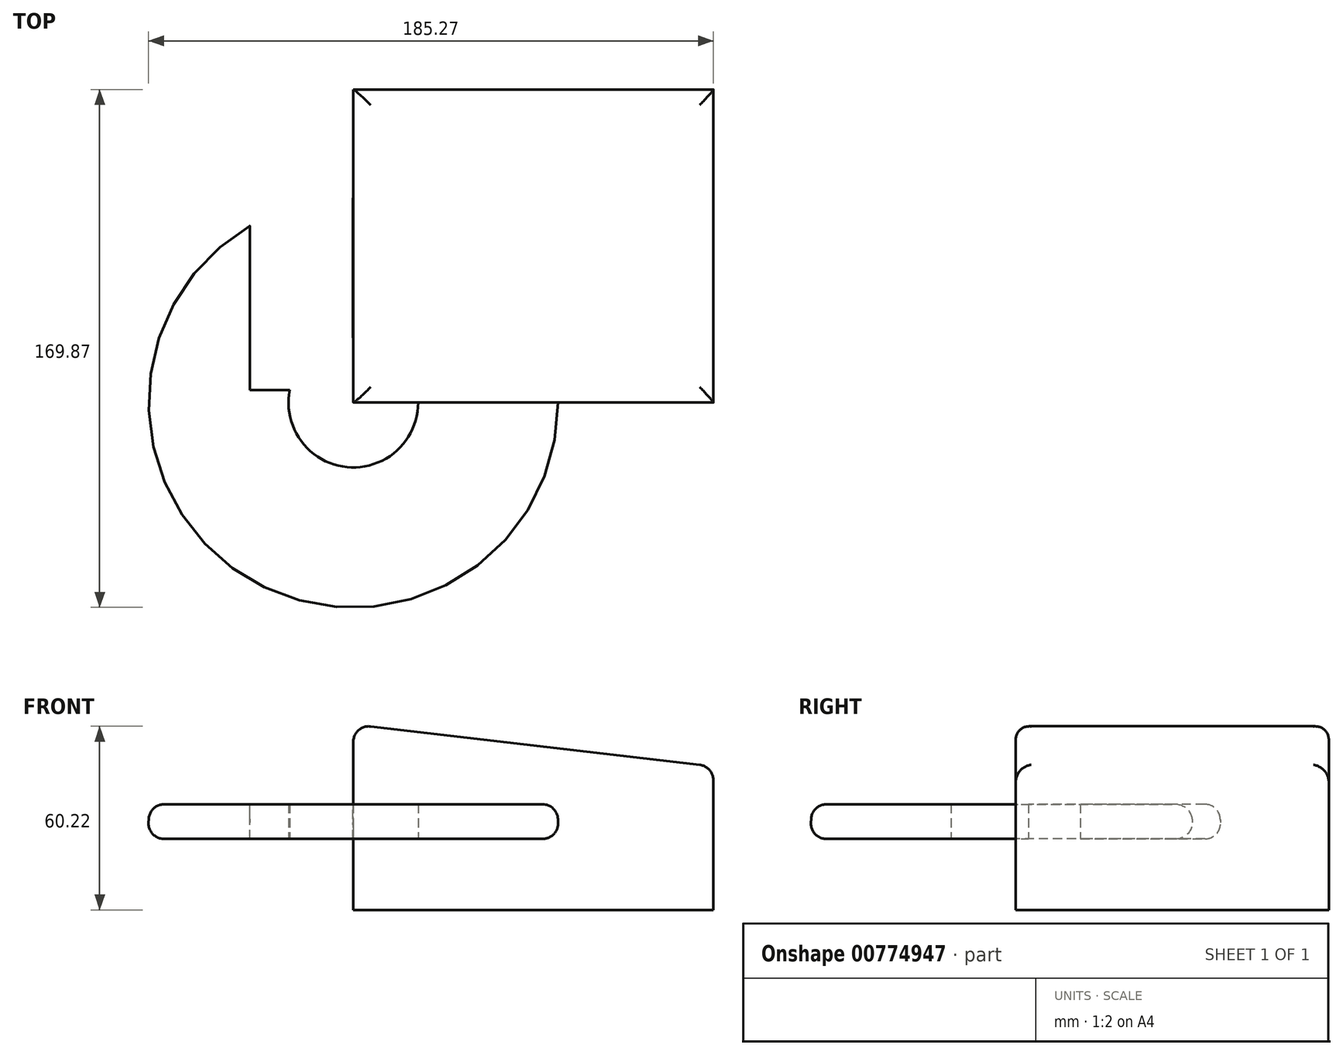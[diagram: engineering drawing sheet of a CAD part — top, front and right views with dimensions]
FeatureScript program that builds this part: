
annotation { "Feature Type Name" : "Feature", "Feature Type Description" : "" }
export const myFeature = defineFeature(function(context is Context, id is Id, definition is map)
    precondition{}
    {
        {
            var Q0;
            Q0=qCreatedBy(makeId("Front.planeOp"),FACE);
            var sketch = newSketch(context, id + "F0", { "sketchPlane" : qUnion([Q0])});
            skLineSegment(sketch, "E0", {"start": v(62.23, 12.4) * mm, "end": v(62.23, -34.65) * mm});
            skLineSegment(sketch, "E1", {"start": v(62.23, -34.65) * mm, "end": v(-55.87, -34.65) * mm});
            skLineSegment(sketch, "E2", {"start": v(-55.87, -34.65) * mm, "end": v(-55.87, 26.2) * mm});
            skLineSegment(sketch, "E3", {"start": v(-55.87, 26.2) * mm, "end": v(62.23, 12.4) * mm});
            skSolve(sketch);
        }
        {
            var Q0;
            Q0=makeQuery(id+"F0.imprint","IMPRINT",FACE,{"disambiguationData":[TD([[makeQuery(id+"F0.imprint","IMPRINT",EDGE,{"derivedFrom":sQuery(id+"F0.wireOp",EDGE,"E0")}),-1.0]])]});
            var Q1;
            Q1 = qSketchRegion(id + "F0", true);
            extrude(context, id + "F1", {"entities" : qUnion([Q0, Q1]), "depth" : 102.7 * mm, "offsetDistance" : 25.4 * mm});
        }
        {
            var Q0;
            Q0=makeQuery(id+"F1.opExtrude","CAP_FACE",FACE,{"disambiguationData":[OSD([sQuery(id+"F0.wireOp",EDGE,"E0"),sQuery(id+"F0.wireOp",EDGE,"E1"),sQuery(id+"F0.wireOp",EDGE,"E2"),sQuery(id+"F0.wireOp",EDGE,"E3")])],"isStart":false});
            var sketch = newSketch(context, id + "F2", { "sketchPlane" : qUnion([Q0])});
            skLineSegment(sketch, "E4", {"start": v(11.54, -11.35) * mm, "end": v(-34.62, -11.35) * mm});
            skLineSegment(sketch, "E5", {"start": v(-34.62, -11.35) * mm, "end": v(-34.62, 0) * mm});
            skLineSegment(sketch, "E6", {"start": v(-34.62, 0) * mm, "end": v(11.03, 0) * mm});
            skLineSegment(sketch, "E7", {"start": v(11.03, 0) * mm, "end": v(11.54, -11.35) * mm});
            skSolve(sketch);
        }
        {
            var Q0;
            Q0 = qSketchRegion(id + "F2", true);
            var Q1;
            Q1=makeQuery(id+"F1.opExtrude","CAP_EDGE",EDGE,{"disambiguationData":[OSD([sQuery(id+"F0.wireOp",EDGE,"E2")])],"isStart":false});
            revolve(context, id + "F3", {"operationType" : NewBodyOperationType.ADD, "surfaceOperationType" : NewSurfaceOperationType.NEW, "entities" : qUnion([Q0]), "axis" : qUnion([Q1]), "revolveType" : RevolveType.FULL});
        }
        {
            var Q0;
            Q0=makeQuery(id+"F1.opExtrude","SWEPT_FACE",FACE,{"disambiguationData":[OSD([sQuery(id+"F0.wireOp",EDGE,"E3")])]});
            var Q1;
            Q1=makeQuery(id+"F3.opRevolve","SWEPT_EDGE",EDGE,{"disambiguationData":[OSD([sQuery(id+"F2.wireOp",EDGE,"E6"),sQuery(id+"F2.wireOp",EDGE,"E7")])]});
            var Q2;
            Q2=makeQuery(id+"F3.opRevolve","SWEPT_EDGE",EDGE,{"disambiguationData":[OSD([sQuery(id+"F2.wireOp",EDGE,"E4"),sQuery(id+"F2.wireOp",EDGE,"E7")])]});
            fillet(context, id + "F4", {"entities" : qUnion([Q0, Q1, Q2]), "radius" : 5.08 * mm, "tangentPropagation" : true, "allowEdgeOverflow" : false});
        }
        {
            var Q0;
            Q0=qCreatedBy(makeId("Top.planeOp"),FACE);
            var sketch = newSketch(context, id + "F5", { "sketchPlane" : qUnion([Q0])});
            skLineSegment(sketch, "E8.bottom", {"start": v(-89.8, -33) * mm, "end": v(-56.06, -33) * mm});
            skLineSegment(sketch, "E8.top", {"start": v(-89.8, -98.56) * mm, "end": v(-56.06, -98.56) * mm});
            skLineSegment(sketch, "E8.left", {"start": v(-89.8, -33) * mm, "end": v(-89.8, -98.56) * mm});
            skLineSegment(sketch, "E8.right", {"start": v(-56.06, -33) * mm, "end": v(-56.06, -98.56) * mm});
            skSolve(sketch);
        }
        {
            var Q0;
            Q0 = qSketchRegion(id + "F5", true);
            extrude(context, id + "F6", {"entities" : qUnion([Q0]), "operationType" : NewBodyOperationType.REMOVE, "oppositeDirection" : true, "depth" : 25.4 * mm, "offsetDistance" : 25.4 * mm});
        }
    });
